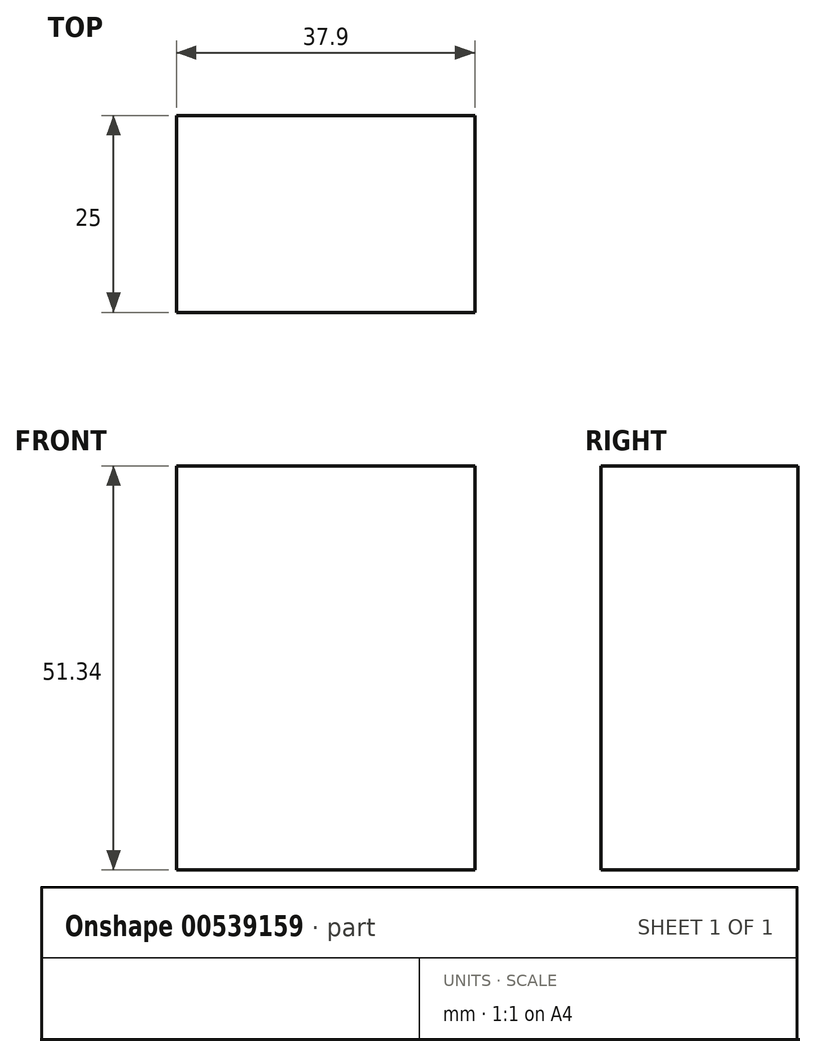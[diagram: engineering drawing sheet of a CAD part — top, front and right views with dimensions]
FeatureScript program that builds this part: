
annotation { "Feature Type Name" : "Feature", "Feature Type Description" : "" }
export const myFeature = defineFeature(function(context is Context, id is Id, definition is map)
    precondition{}
    {
        {
            var Q0;
            Q0=qCreatedBy(makeId("Front.planeOp"),FACE);
            var sketch = newSketch(context, id + "F0", { "sketchPlane" : qUnion([Q0])});
            skLineSegment(sketch, "E0.bottom", {"start": v(-158.4, 76.17) * mm, "end": v(-120.5, 76.17) * mm});
            skLineSegment(sketch, "E0.top", {"start": v(-158.4, 24.83) * mm, "end": v(-120.5, 24.83) * mm});
            skLineSegment(sketch, "E0.left", {"start": v(-158.4, 76.17) * mm, "end": v(-158.4, 24.83) * mm});
            skLineSegment(sketch, "E0.right", {"start": v(-120.5, 76.17) * mm, "end": v(-120.5, 24.83) * mm});
            skSolve(sketch);
        }
        {
            var Q0;
            Q0 = qSketchRegion(id + "F0", true);
            extrude(context, id + "F1", {"entities" : qUnion([Q0]), "depth" : 25 * mm, "offsetDistance" : 25 * mm});
        }
    });
